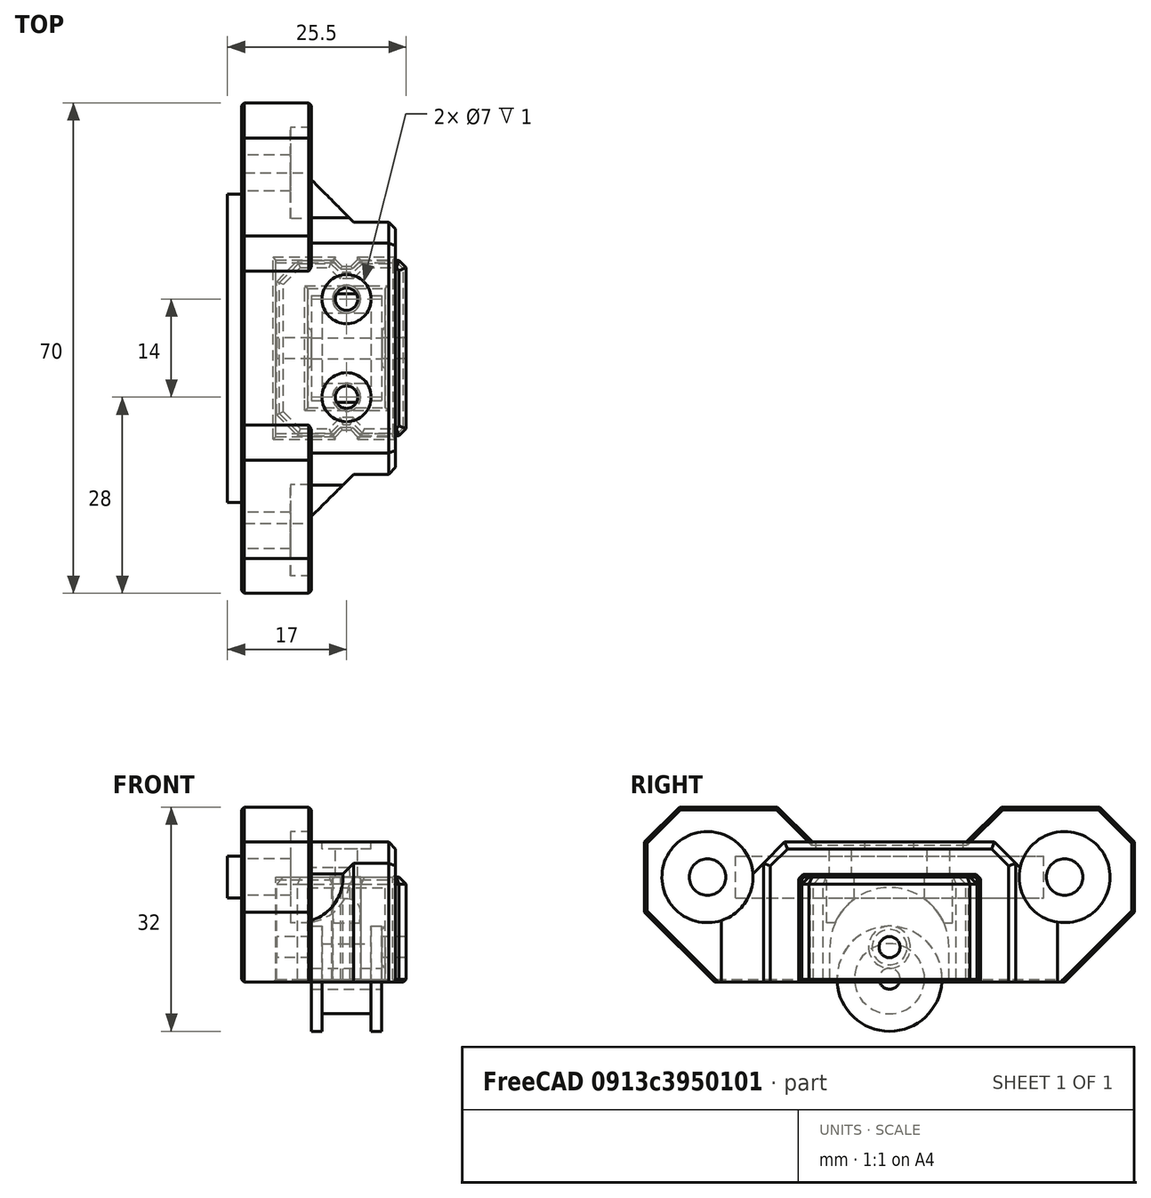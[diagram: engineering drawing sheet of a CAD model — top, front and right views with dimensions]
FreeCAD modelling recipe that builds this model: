
FCSTD DOCUMENT  (FreeCAD 0.18R16146 (Git))
Label: idler-tensioner
License: All rights reserved
LicenseURL: http://en.wikipedia.org/wiki/All_rights_reserved
objects: Part::Chamfer×19, Part::MultiFuse×14, Part::Box×11, Part::Cylinder×10, Part::Cut×7, Part::Feature×3, App::Part×2
note: 64 computed .brp shape members not serialized (recipe doc carries the construction recipe); baked Part::Feature solids carry a one-line shape summary decoded from their .brp

FEATURE [Part::Feature] Cut001001001  label="16t-idler"
  Placement = pos=(0,0,0.5) rot=(0,0,1;0rad)
  shape: bbox 10 x 15 x 15 mm, 8 faces (baked)
FEATURE [Part::Box] Box  label="Cube"
  AttacherType = Attacher::AttachEngine3D
  Height = 15
  Length = 18.5
  Placement = pos=(-10,-12.5,0) rot=(0,0,1;0rad)
  Width = 25
FEATURE [Part::Cylinder] Cylinder
  Angle = 360
  AttacherType = Attacher::AttachEngine3D
  Height = 22
  Placement = pos=(11,0,5) rot=(0,-1,0;1.5708rad)
  Radius = 1.5
FEATURE [Part::Cylinder] Cylinder001
  Angle = 360
  AttacherType = Attacher::AttachEngine3D
  Height = 11.1
  Placement = pos=(-5.55,0,5) rot=(0,1,0;1.5708rad)
  Radius = 8.5
FEATURE [Part::Box] Box001  label="Cube001"
  AttacherType = Attacher::AttachEngine3D
  Height = 5
  Length = 11.1
  Placement = pos=(-5.55,-8.5,0) rot=(0,0,1;0rad)
  Width = 17
FEATURE [Part::Cylinder] Cylinder003
  Angle = 360
  AttacherType = Attacher::AttachEngine3D
  Height = 10
  Placement = pos=(0,-7,8.5) rot=(0,0,1;0rad)
  Radius = 2
FEATURE [Part::Box] Box002  label="Cube002"
  AttacherType = Attacher::AttachEngine3D
  Height = 21
  Length = 4.2
  Placement = pos=(-2.1,-21,0) rot=(0,0,1;0rad)
  Width = 10.1
FEATURE [Part::Box] Box003  label="Cube003"
  AttacherType = Attacher::AttachEngine3D
  Height = 21
  Length = 4.2
  Placement = pos=(-2.1,10.9,0) rot=(0,0,1;0rad)
  Width = 10.1
FEATURE [Part::Cylinder] Cylinder004
  Angle = 360
  AttacherType = Attacher::AttachEngine3D
  Height = 1
  Placement = pos=(5.05,0,5) rot=(0,1,0;1.5708rad)
  Radius = 3
FEATURE [Part::Cylinder] Cylinder005
  Angle = 360
  AttacherType = Attacher::AttachEngine3D
  Height = 1
  Placement = pos=(-6.05,0,5) rot=(0,1,0;1.5708rad)
  Radius = 3
FEATURE [Part::Box] Box004  label="Cube004"
  AttacherType = Attacher::AttachEngine3D
  Height = 20
  Length = 22
  Placement = pos=(-15,-18,0) rot=(0,0,1;0rad)
  Width = 36
FEATURE [Part::Box] Box005  label="Cube005"
  AttacherType = Attacher::AttachEngine3D
  Height = 15
  Length = 20.2
  Placement = pos=(-10.1,-12.6,0) rot=(0,0,1;0rad)
  Width = 25.2
FEATURE [Part::Box] Box006  label="Cube006"
  AttacherType = Attacher::AttachEngine3D
  Height = 15
  Length = 4
  Placement = pos=(-2,11.3,0) rot=(0,0,1;0rad)
  Width = 1.7
FEATURE [Part::Box] Box007  label="Cube007"
  AttacherType = Attacher::AttachEngine3D
  Height = 15
  Length = 4
  Placement = pos=(-2,-13,0) rot=(0,0,1;0rad)
  Width = 1.7
FEATURE [Part::Cylinder] Cylinder006
  Angle = 360
  AttacherType = Attacher::AttachEngine3D
  Height = 10
  Placement = pos=(0,0,29) rot=(0,0,1;0rad)
  Radius = 3.5
FEATURE [Part::Cylinder] Cylinder007
  Angle = 360
  AttacherType = Attacher::AttachEngine3D
  Height = 12
  Placement = pos=(0,0,19) rot=(0,0,1;0rad)
  Radius = 1.6
FEATURE [Part::Box] Box008  label="Cube008"
  AttacherType = Attacher::AttachEngine3D
  Height = 6
  Length = 3
  Placement = pos=(-17,-22,12) rot=(0,0,1;0rad)
  Width = 44
FEATURE [Part::MultiFuse] Fusion
  Shapes = -> [Cylinder001,Box001]
FEATURE [Part::Chamfer] Chamfer003008
  Base = -> Box002
  Edges = 2 edges r=1.6: [Edge3,Edge7]
FEATURE [Part::Chamfer] Chamfer003009
  Base = -> Box003
  Edges = 2 edges r=1.6: [Edge1,Edge5]
FEATURE [Part::Cut] Cut
  Base = -> Box
  Tool = -> Fusion
FEATURE [Part::Cylinder] Cylinder008
  Angle = 360
  AttacherType = Attacher::AttachEngine3D
  Height = 10
  Placement = pos=(0,7,8.5) rot=(0,0,1;0rad)
  Radius = 2
FEATURE [Part::MultiFuse] Fusion007
  Shapes = -> [Cylinder003,Cylinder008]
FEATURE [Part::Cut] Cut001001009
  Base = -> Cut
  Tool = -> Fusion007
FEATURE [Part::MultiFuse] Fusion008
  Shapes = -> [Chamfer003008,Chamfer003009]
FEATURE [Part::Cut] Cut001001010
  Base = -> Cut001001009
  Tool = -> Fusion008
FEATURE [Part::Chamfer] Chamfer003010
  Base = -> Cut001001010
  Edges = 2 edges r=3: [Edge1,Edge3]
FEATURE [Part::Chamfer] Chamfer003011
  Base = -> Chamfer003010
  Edges = 2 edges r=1: [Edge48,Edge50]
FEATURE [Part::Chamfer] Chamfer003012
  Base = -> Chamfer003011
  Edges = 16 edges r=1: [Edge1,Edge2,Edge3,Edge4,Edge5,Edge6,Edge7,Edge8,Edge9,Edge10,Edge11,Edge12,Edge13,Edge14,Edge15,Edge16]
FEATURE [Part::Chamfer] Chamfer003015
  Base = -> Chamfer003012
  Edges = 24 edges r=0.4: [Edge60,Edge63,Edge64,Edge66,Edge69,Edge70,Edge72,Edge75,Edge76,Edge79,Edge81,Edge83,Edge84,Edge86,Edge88,Edge90,Edge97,Edge98,Edge99,Edge100,Edge101,Edge102,Edge103,Edge104]
FEATURE [Part::MultiFuse] Fusion011
  Shapes = -> [Box007,Box006]
FEATURE [Part::Chamfer] Chamfer
  Base = -> Fusion011
  Edges = 4 edges r=1.2: [Edge3,Edge7,Edge13,Edge17]
FEATURE [Part::MultiFuse] Fusion013
  Placement = pos=(0,-7,-10) rot=(0,0,1;0rad)
  Shapes = -> [Cylinder006,Cylinder007]
FEATURE [Part::Feature] Fusion013001  label="Fusion014"
  Placement = pos=(0,7,-10) rot=(0,0,1;0rad)
  shape: bbox 7 x 7 x 20 mm, 5 faces (baked)
FEATURE [Part::MultiFuse] Fusion013002
  Shapes = -> [Fusion013001,Fusion013]
FEATURE [Part::Box] Box009  label="Cube009"
  AttacherType = Attacher::AttachEngine3D
  Height = 25
  Length = 10
  Placement = pos=(-15,-35,0) rot=(0,0,1;0rad)
  Width = 24
FEATURE [Part::Box] Box010  label="Cube010"
  AttacherType = Attacher::AttachEngine3D
  Height = 25
  Length = 10
  Placement = pos=(-15,11,0) rot=(0,0,1;0rad)
  Width = 24
FEATURE [Part::MultiFuse] Fusion013004
  Shapes = -> [Box009,Box010]
FEATURE [Part::Cylinder] Cylinder009
  Angle = 360
  AttacherType = Attacher::AttachEngine3D
  Height = 10
  Radius = 2.6
FEATURE [Part::Cylinder] Cylinder010
  Angle = 360
  AttacherType = Attacher::AttachEngine3D
  Height = 10
  Placement = pos=(0,0,-10) rot=(0,0,1;0rad)
  Radius = 6.5
FEATURE [Part::Chamfer] Chamfer003021
  Base = -> Box004
  Edges = 2 edges r=3: [Edge10,Edge12]
FEATURE [Part::Chamfer] Chamfer003022
  Base = -> Chamfer003021
  Edges = 5 edges r=1: [Edge7,Edge11,Edge15,Edge16,Edge18]
FEATURE [Part::Chamfer] Chamfer003024
  Base = -> Chamfer003022
  Edges = 6 edges r=0.4: [Edge3,Edge6,Edge11,Edge12,Edge13,Edge14]
FEATURE [Part::Chamfer] Chamfer003027
  Base = -> Chamfer
  Edges = 10 edges r=0.4: [Edge4,Edge10,Edge14,Edge15,Edge16,Edge22,Edge28,Edge32,Edge33,Edge34]
FEATURE [Part::MultiFuse] Fusion013005006
  Shapes = -> [Cylinder005,Cylinder004]
FEATURE [Part::Chamfer] Chamfer003028
  Base = -> Fusion013005006
  Edges = 2 edges r=0.5: [Edge1,Edge6]
FEATURE [Part::MultiFuse] Fusion013005007
  Shapes = -> [Chamfer003028,Chamfer003015]
FEATURE [Part::Cut] Cut001001017
  Base = -> Fusion013005007
  Tool = -> Cylinder
FEATURE [App::Part] Part001  label="idler-inner"
  Group = -> [Box001,Cylinder004,Cut001001009,Box003,Chamfer003015,Box002,Box,Fusion,Cylinder005,Chamfer003009,Cylinder008,Cylinder001,Fusion007,Cylinder,Cut001001010,Cylinder003,Chamfer003010,Chamfer003012,Fusion008,Chamfer003011,Chamfer003008,Cut,Fusion013005006,Fusion013005007,Chamfer003028,Cut001001017]
  Origin = -> Origin001
  Placement = pos=(0,0,-4) rot=(0,0,1;0rad)
FEATURE [Part::Chamfer] Chamfer003029
  Base = -> Fusion013004
  Edges = 2 edges r=5: [Edge12,Edge22]
FEATURE [Part::Chamfer] Chamfer003030
  Base = -> Chamfer003029
  Edges = 2 edges r=5: [Edge7,Edge28]
FEATURE [Part::Chamfer] Chamfer003031
  Base = -> Chamfer003030
  Edges = 2 edges r=10: [Edge15,Edge33]
FEATURE [Part::Chamfer] Chamfer003032
  Base = -> Chamfer003031
  Edges = 22 edges r=0.4: [Edge1,Edge2,Edge3,Edge4,Edge5,Edge7,Edge8,Edge12,Edge14,Edge18,Edge21,Edge22,Edge23,Edge24,Edge25,Edge26,Edge28,Edge29,Edge33,Edge35,Edge39,Edge42]
FEATURE [Part::MultiFuse] Fusion013005008
  Shapes = -> [Chamfer003032,Chamfer003024]
FEATURE [Part::Chamfer] Chamfer003033
  Base = -> Fusion013005008
  Edges = 2 edges r=6: [Edge87,Edge89]
FEATURE [Part::Cut] Cut001001018
  Base = -> Chamfer003033
  Tool = -> Box005
FEATURE [Part::Chamfer] Chamfer003034
  Base = -> Cut001001018
  Edges = 2 edges r=0.4: [Edge64,Edge119]
FEATURE [Part::Chamfer] Chamfer003035
  Base = -> Chamfer003034
  Edges = 12 edges r=0.4: [Edge1,Edge2,Edge4,Edge6,Edge8,Edge14,Edge16,Edge31,Edge33,Edge44,Edge45,Edge46]
FEATURE [Part::MultiFuse] Fusion013005009
  Shapes = -> [Chamfer003035,Chamfer003027]
FEATURE [Part::Cut] Cut001001019
  Base = -> Fusion013005009
  Tool = -> Fusion013002
FEATURE [Part::MultiFuse] Fusion013005010
  Shapes = -> [Box008,Cut001001019]
FEATURE [Part::MultiFuse] Fusion013005011
  Placement = pos=(-8,-26,15) rot=(0,1,0;4.71239rad)
  Shapes = -> [Cylinder009,Cylinder010]
FEATURE [Part::Feature] Fusion013005011001  label="Fusion013005012"
  Placement = pos=(-8,25,15) rot=(0,-1,0;1.5708rad)
  shape: bbox 20 x 13 x 13 mm, 5 faces (baked)
FEATURE [Part::MultiFuse] Fusion013005011002
  Shapes = -> [Fusion013005011001,Fusion013005011]
FEATURE [Part::Cut] Cut001001020
  Base = -> Fusion013005010
  Tool = -> Fusion013005011002
FEATURE [App::Part] Part  label="idler-outer"
  Group = -> [Box010,Box004,Fusion013004,Chamfer003027,Box006,Box008,Chamfer003024,Box007,Box005,Cylinder007,Cylinder006,Box009,Fusion013001,Cylinder010,Fusion011,Chamfer,Chamfer003021,Fusion013,Fusion013002,Cylinder009,Chamfer003022,Cut001001018,Chamfer003033,Fusion013005008,Chamfer003029,Chamfer003030,Chamfer003031,Chamfer003032,Fusion013005009,Fusion013005011002,Fusion013005010,Chamfer003035,Chamfer003034,+4 more]
  Origin = -> Origin
